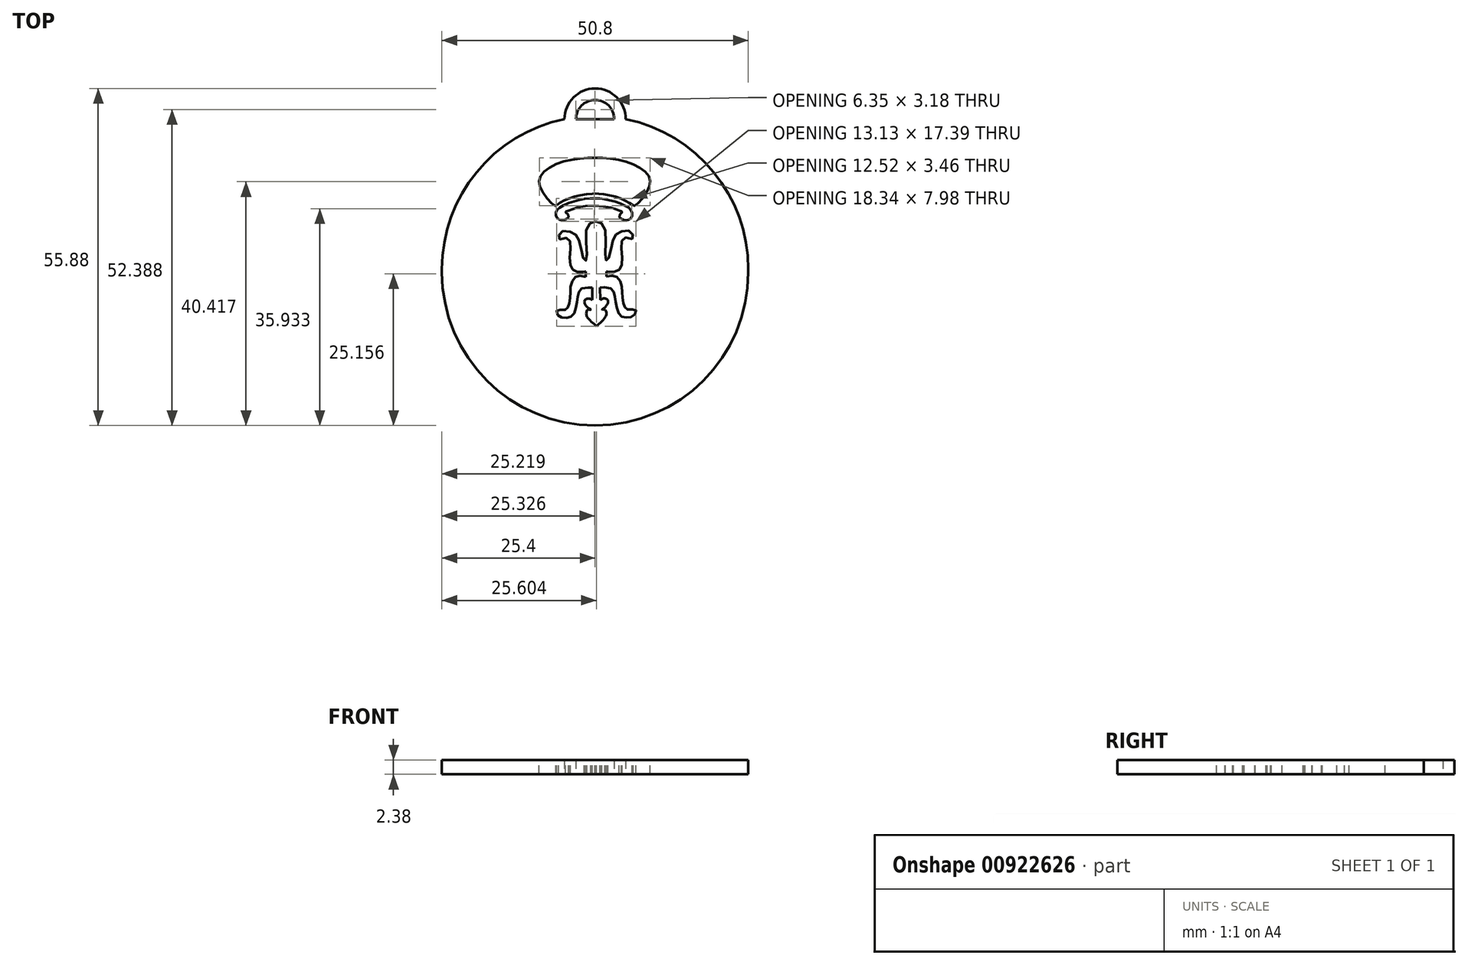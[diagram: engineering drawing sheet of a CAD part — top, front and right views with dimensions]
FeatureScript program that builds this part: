
annotation { "Feature Type Name" : "Feature", "Feature Type Description" : "" }
export const myFeature = defineFeature(function(context is Context, id is Id, definition is map)
    precondition{}
    {
        {
            var Q0;
            Q0=qCreatedBy(makeId("Top.planeOp"),FACE);
            var sketch = newSketch(context, id + "F0", { "sketchPlane" : qUnion([Q0])});
            skLineSegment(sketch, "E0.bottom", {"start": v(-25.4, 25.4) * mm, "end": v(25.4, 25.4) * mm});
            skLineSegment(sketch, "E0.top", {"start": v(-25.4, -25.4) * mm, "end": v(25.4, -25.4) * mm});
            skLineSegment(sketch, "E0.left", {"start": v(-25.4, 25.4) * mm, "end": v(-25.4, -25.4) * mm});
            skLineSegment(sketch, "E0.right", {"start": v(25.4, 25.4) * mm, "end": v(25.4, -25.4) * mm});
            skSolve(sketch);
        }
        {
            var Q0;
            Q0=makeQuery(id+"F0.imprint","IMPRINT",FACE,{"disambiguationData":[TD([[makeQuery(id+"F0.imprint","IMPRINT",EDGE,{"derivedFrom":sQuery(id+"F0.wireOp",EDGE,"E0.bottom")}),-1.0]])]});
            extrude(context, id + "F1", {"entities" : qUnion([Q0]), "endBound" : BoundingType.SYMMETRIC, "depth" : 2.38 * mm, "offsetDistance" : 25.4 * mm});
        }
        {
            var Q0;
            Q0=makeQuery(id+"F1.opExtrude","CAP_FACE",FACE,{"disambiguationData":[OSD([sQuery(id+"F0.wireOp",EDGE,"E0.bottom"),sQuery(id+"F0.wireOp",EDGE,"E0.top"),sQuery(id+"F0.wireOp",EDGE,"E0.left"),sQuery(id+"F0.wireOp",EDGE,"E0.right")])],"isStart":false});
            var sketch = newSketch(context, id + "F2", { "sketchPlane" : qUnion([Q0])});
            skFitSpline(sketch, "E1", {"points": [v(-0.02, 12.26) * mm, v(-3.27, 11.83) * mm, v(-6.05, 10.61) * mm, v(-6.5, 9.74) * mm, v(-6.2, 8.87) * mm, v(-4.98, 8.7) * mm, v(-4.4, 9.41) * mm, v(-4.89, 9.98) * mm, v(-4.6, 10.16) * mm, v(-0.1, 11.04) * mm], "startDerivative": vector(-18.9, 0.47) * mm, "endDerivative": vector(38.49, -0.86) * mm});
            skFitSpline(sketch, "E2.MirrorCS", {"points": [v(-0.02, 12.26) * mm, v(2.9, 11.83) * mm, v(5.67, 10.61) * mm, v(6.13, 9.74) * mm, v(5.82, 8.87) * mm, v(4.6, 8.7) * mm, v(4.02, 9.41) * mm, v(4.51, 9.98) * mm, v(4.23, 10.15) * mm, v(-0.1, 11.04) * mm], "startDerivative": vector(18.9, 0.47) * mm, "endDerivative": vector(-38.49, 0.86) * mm});
            skFitSpline(sketch, "E3", {"points": [v(0.03, 19) * mm, v(-5.4, 18.33) * mm, v(-8.98, 16.06) * mm, v(-8.95, 13.72) * mm, v(-6.7, 11.04) * mm, v(-6.3, 11.2) * mm, v(-4.73, 12.1) * mm, v(-2, 12.86) * mm, v(0.03, 13.04) * mm], "startDerivative": vector(-27.52, -0.97) * mm, "endDerivative": vector(2.4, 0.01) * mm});
            skFitSpline(sketch, "E4.MirrorCS", {"points": [v(0.03, 19) * mm, v(5.25, 18.33) * mm, v(8.83, 16.06) * mm, v(8.8, 13.72) * mm, v(6.56, 11.03) * mm, v(6.14, 11.2) * mm, v(4.57, 12.1) * mm, v(1.83, 12.87) * mm, v(0.03, 13.04) * mm], "startDerivative": vector(27.52, -0.97) * mm, "endDerivative": vector(-7.43, -0.03) * mm});
            skSolve(sketch);
        }
        {
            var Q0;
            Q0=makeQuery(id+"F2.imprint","IMPRINT",FACE,{"disambiguationData":[TD([[makeQuery(id+"F2.imprint","IMPRINT",EDGE,{"derivedFrom":sQuery(id+"F2.wireOp",EDGE,"E3")}),1.0]])]});
            var Q1;
            Q1=makeQuery(id+"F2.imprint","IMPRINT",FACE,{"disambiguationData":[TD([[makeQuery(id+"F2.imprint","IMPRINT",EDGE,{"derivedFrom":sQuery(id+"F2.wireOp",EDGE,"E1")}),1.0]])]});
            var Q2;
            Q2=makeQuery(id+"F1.opExtrude","CAP_FACE",FACE,{"disambiguationData":[OSD([sQuery(id+"F0.wireOp",EDGE,"E0.bottom"),sQuery(id+"F0.wireOp",EDGE,"E0.top"),sQuery(id+"F0.wireOp",EDGE,"E0.left"),sQuery(id+"F0.wireOp",EDGE,"E0.right")])],"isStart":false});
            extrude(context, id + "F3", {"entities" : qUnion([Q0, Q1]), "operationType" : NewBodyOperationType.REMOVE, "endBound" : BoundingType.SYMMETRIC, "oppositeDirection" : true, "depth" : 12.7 * mm, "endBoundEntityFace" : qUnion([Q2]), "offsetDistance" : 25.4 * mm});
        }
        {
            var Q0;
            Q0=makeQuery(id+"F1.opExtrude","CAP_FACE",FACE,{"disambiguationData":[OSD([sQuery(id+"F0.wireOp",EDGE,"E0.bottom"),sQuery(id+"F0.wireOp",EDGE,"E0.top"),sQuery(id+"F0.wireOp",EDGE,"E0.left"),sQuery(id+"F0.wireOp",EDGE,"E0.right")])],"isStart":false});
            var sketch = newSketch(context, id + "F4", { "sketchPlane" : qUnion([Q0])});
            skCircle(sketch, "E5", {"center": v(0, 0) * mm, "radius": 15.9 * mm});
            skSolve(sketch);
        }
        {
            var Q0;
            Q0=makeQuery(id+"F1.opExtrude","CAP_FACE",FACE,{"disambiguationData":[OSD([sQuery(id+"F0.wireOp",EDGE,"E0.bottom"),sQuery(id+"F0.wireOp",EDGE,"E0.top"),sQuery(id+"F0.wireOp",EDGE,"E0.left"),sQuery(id+"F0.wireOp",EDGE,"E0.right")])],"isStart":false});
            var sketch = newSketch(context, id + "F5", { "sketchPlane" : qUnion([Q0])});
            skFitSpline(sketch, "E6", {"points": [v(0.12, 8.45) * mm, v(-1.38, 7.32) * mm, v(-1.44, 2.08) * mm, v(-1.76, 2) * mm, v(-2.62, 5.09) * mm, v(-3.64, 6.54) * mm, v(-5.7, 6.65) * mm, v(-5.95, 5.54) * mm, v(-5.47, 5.52) * mm, v(-5.06, 5.7) * mm, v(-4.26, 5.33) * mm, v(-4.2, 2.37) * mm, v(-3.8, 0.54) * mm, v(-2.8, 0.06) * mm, v(-1.67, 0.1) * mm, v(-1.55, 0.13) * mm], "startDerivative": vector(-21.24, 0) * mm, "endDerivative": vector(6.89, -0.37) * mm});
            skLineSegment(sketch, "E7", {"start": v(-1.55, 0.13) * mm, "end": v(-1.55, -0.75) * mm});
            skFitSpline(sketch, "E8", {"points": [v(-1.55, -0.75) * mm, v(-3.2, -0.75) * mm, v(-4.04, -2.3) * mm, v(-4.12, -4.1) * mm, v(-4.47, -5.7) * mm, v(-4.96, -6.26) * mm, v(-6.3, -6.28) * mm, v(-6.11, -7.17) * mm, v(-4.93, -7.55) * mm, v(-3.75, -7.22) * mm, v(-3.1, -5.45) * mm, v(-2.83, -3.81) * mm, v(-2.16, -2.65) * mm, v(-0.45, -2.57) * mm, v(-0.52, -2.57) * mm], "startDerivative": vector(-22.57, 4.7) * mm, "endDerivative": vector(-4.22, 0.19) * mm});
            skLineSegment(sketch, "E9", {"start": v(-0.45, -2.57) * mm, "end": v(-0.45, -4.6) * mm});
            skFitSpline(sketch, "E10", {"points": [v(-0.45, -4.6) * mm, v(-1.69, -4.6) * mm, v(-0.93, -6.04) * mm], "startDerivative": vector(-3.2, 2.32) * mm, "endDerivative": vector(4.4, -3) * mm});
            skFitSpline(sketch, "E11", {"points": [v(-0.93, -6.04) * mm, v(-0.75, -6.22) * mm, v(-1.2, -6.2) * mm, v(-1.45, -6.78) * mm, v(-1.1, -7.7) * mm, v(0.22, -8.94) * mm], "startDerivative": vector(2.9, -1.98) * mm, "endDerivative": vector(0.65, -0.42) * mm});
            skFitSpline(sketch, "E12.MirrorCS", {"points": [v(0.12, 8.45) * mm, v(1.63, 7.34) * mm, v(1.74, 2.1) * mm, v(2.06, 2.02) * mm, v(2.89, 5.12) * mm, v(3.9, 6.58) * mm, v(5.96, 6.71) * mm, v(6.22, 5.62) * mm, v(5.73, 5.58) * mm, v(5.33, 5.77) * mm, v(4.52, 5.38) * mm, v(4.5, 2.42) * mm, v(4.12, 0.6) * mm, v(3.14, 0.1) * mm, v(2, 0.12) * mm, v(1.87, 0.15) * mm], "startDerivative": vector(21.24, 0.25) * mm, "endDerivative": vector(-6.88, -0.45) * mm});
            skLineSegment(sketch, "E13.MirrorCS", {"start": v(1.87, 0.15) * mm, "end": v(1.89, -0.73) * mm});
            skFitSpline(sketch, "E14.MirrorCS", {"points": [v(1.89, -0.73) * mm, v(3.55, -0.71) * mm, v(4.4, -2.26) * mm, v(4.5, -4.06) * mm, v(4.87, -5.64) * mm, v(5.36, -6.2) * mm, v(6.7, -6.2) * mm, v(6.53, -7.1) * mm, v(5.35, -7.49) * mm, v(4.16, -7.18) * mm, v(3.5, -5.41) * mm, v(3.2, -3.77) * mm, v(2.52, -2.63) * mm, v(0.8, -2.57) * mm, v(0.88, -2.57) * mm], "startDerivative": vector(22.51, 4.96) * mm, "endDerivative": vector(4.22, 0.24) * mm});
            skLineSegment(sketch, "E15.MirrorCS", {"start": v(0.8, -2.57) * mm, "end": v(0.83, -4.59) * mm});
            skFitSpline(sketch, "E16.MirrorCS", {"points": [v(0.83, -4.59) * mm, v(2.07, -4.57) * mm, v(1.33, -6.03) * mm], "startDerivative": vector(3.17, 2.36) * mm, "endDerivative": vector(-4.37, -3.05) * mm});
            skFitSpline(sketch, "E17.MirrorCS", {"points": [v(1.33, -6.03) * mm, v(1.15, -6.2) * mm, v(1.6, -6.18) * mm, v(1.86, -6.76) * mm, v(1.52, -7.68) * mm, v(0.22, -8.94) * mm], "startDerivative": vector(-2.88, -2.01) * mm, "endDerivative": vector(-0.64, -0.43) * mm});
            skSolve(sketch);
        }
        {
            var Q0;
            Q0=makeQuery(id+"F5.imprint","IMPRINT",FACE,{"disambiguationData":[TD([[makeQuery(id+"F5.imprint","IMPRINT",EDGE,{"derivedFrom":sQuery(id+"F5.wireOp",EDGE,"E6")}),1.0]])]});
            extrude(context, id + "F6", {"entities" : qUnion([Q0]), "operationType" : NewBodyOperationType.REMOVE, "oppositeDirection" : true, "depth" : 25.4 * mm, "offsetDistance" : 25.4 * mm});
        }
        {
            var Q0;
            Q0=qCreatedBy(makeId("Top.planeOp"),FACE);
            var sketch = newSketch(context, id + "F7", { "sketchPlane" : qUnion([Q0])});
            skCircle(sketch, "E18", {"center": v(0, 25.4) * mm, "radius": 5.08 * mm});
            skCircle(sketch, "E19", {"center": v(0, 25.4) * mm, "radius": 3.18 * mm});
            skSolve(sketch);
        }
        {
            var Q0;
            Q0=makeQuery(id+"F7.imprint","IMPRINT",FACE,{"disambiguationData":[TD([[makeQuery(id+"F7.imprint","IMPRINT",EDGE,{"derivedFrom":sQuery(id+"F7.wireOp",EDGE,"E18")}),1.0]])]});
            extrude(context, id + "F8", {"entities" : qUnion([Q0]), "operationType" : NewBodyOperationType.ADD, "endBound" : BoundingType.SYMMETRIC, "depth" : 2.38 * mm, "offsetDistance" : 25.4 * mm});
        }
        {
            var Q0;
            Q0=makeQuery(id+"F1.opExtrude","SWEPT_EDGE",EDGE,{"disambiguationData":[OSD([sQuery(id+"F0.wireOp",EDGE,"E0.bottom"),sQuery(id+"F0.wireOp",EDGE,"E0.right")])]});
            var Q1;
            Q1=makeQuery(id+"F1.opExtrude","SWEPT_EDGE",EDGE,{"disambiguationData":[OSD([sQuery(id+"F0.wireOp",EDGE,"E0.bottom"),sQuery(id+"F0.wireOp",EDGE,"E0.left")])]});
            var Q2;
            Q2=makeQuery(id+"F1.opExtrude","SWEPT_EDGE",EDGE,{"disambiguationData":[OSD([sQuery(id+"F0.wireOp",EDGE,"E0.top"),sQuery(id+"F0.wireOp",EDGE,"E0.left")])]});
            var Q3;
            Q3=makeQuery(id+"F1.opExtrude","SWEPT_EDGE",EDGE,{"disambiguationData":[OSD([sQuery(id+"F0.wireOp",EDGE,"E0.top"),sQuery(id+"F0.wireOp",EDGE,"E0.right")])]});
            fillet(context, id + "F9", {"entities" : qUnion([Q0, Q1, Q2, Q3]), "radius" : 25.4 * mm, "tangentPropagation" : true, "allowEdgeOverflow" : false});
        }
    });
